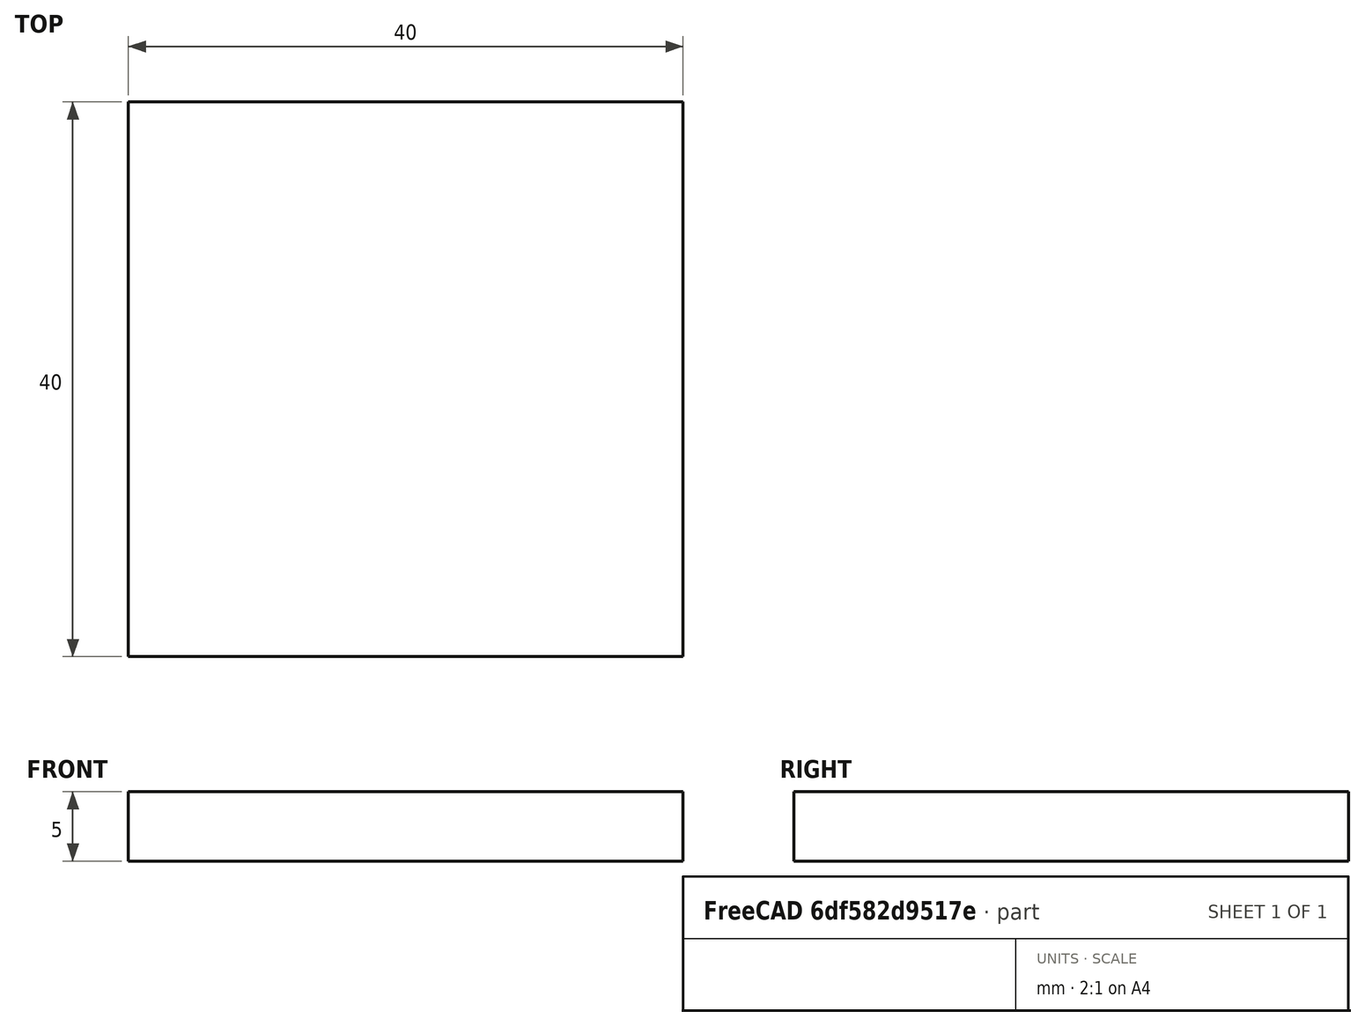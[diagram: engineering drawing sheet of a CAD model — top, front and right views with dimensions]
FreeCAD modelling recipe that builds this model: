
FCSTD DOCUMENT  (FreeCAD 0.18R16110 (Git))
Label: sqware_pad
License: All rights reserved
LicenseURL: http://en.wikipedia.org/wiki/All_rights_reserved
objects: Sketcher::SketchObject×1, PartDesign::Pad×1, PartDesign::Body×1
note: 4 computed .brp shape members not serialized (recipe doc carries the construction recipe); baked Part::Feature solids carry a one-line shape summary decoded from their .brp

FEATURE [Sketcher::SketchObject] Sketch
  MapMode = 5
  Support = -> [XY_Plane]
  sketch-geometry (4):
    g0: LineSegment StartX=0 StartY=0 StartZ=0 EndX=40 EndY=0 EndZ=0
    g1: LineSegment StartX=40 StartY=0 StartZ=0 EndX=40 EndY=40 EndZ=0
    g2: LineSegment StartX=40 StartY=40 StartZ=0 EndX=0 EndY=40 EndZ=0
    g3: LineSegment StartX=0 StartY=40 StartZ=0 EndX=0 EndY=0 EndZ=0
  constraints (11):
    c: Coincident(g0,g1)
    c: Coincident(g1,g2)
    c: Coincident(g2,g3)
    c: Coincident(g3,g0)
    c: Horizontal(g0)
    c: Horizontal(g2)
    c: Vertical(g1)
    c: Vertical(g3)
    c: Coincident(g0,g-1)
    c: DistanceX(g2,g2) = 40
    c: DistanceY(g3,g3) = 40
FEATURE [PartDesign::Pad] Pad
  Length = 5
  Length2 = 100
  Profile = -> Sketch
  Type = 0
FEATURE [PartDesign::Body] Body
  Group = -> [Sketch,Pad]
  Origin = -> Origin
  Tip = -> Pad
